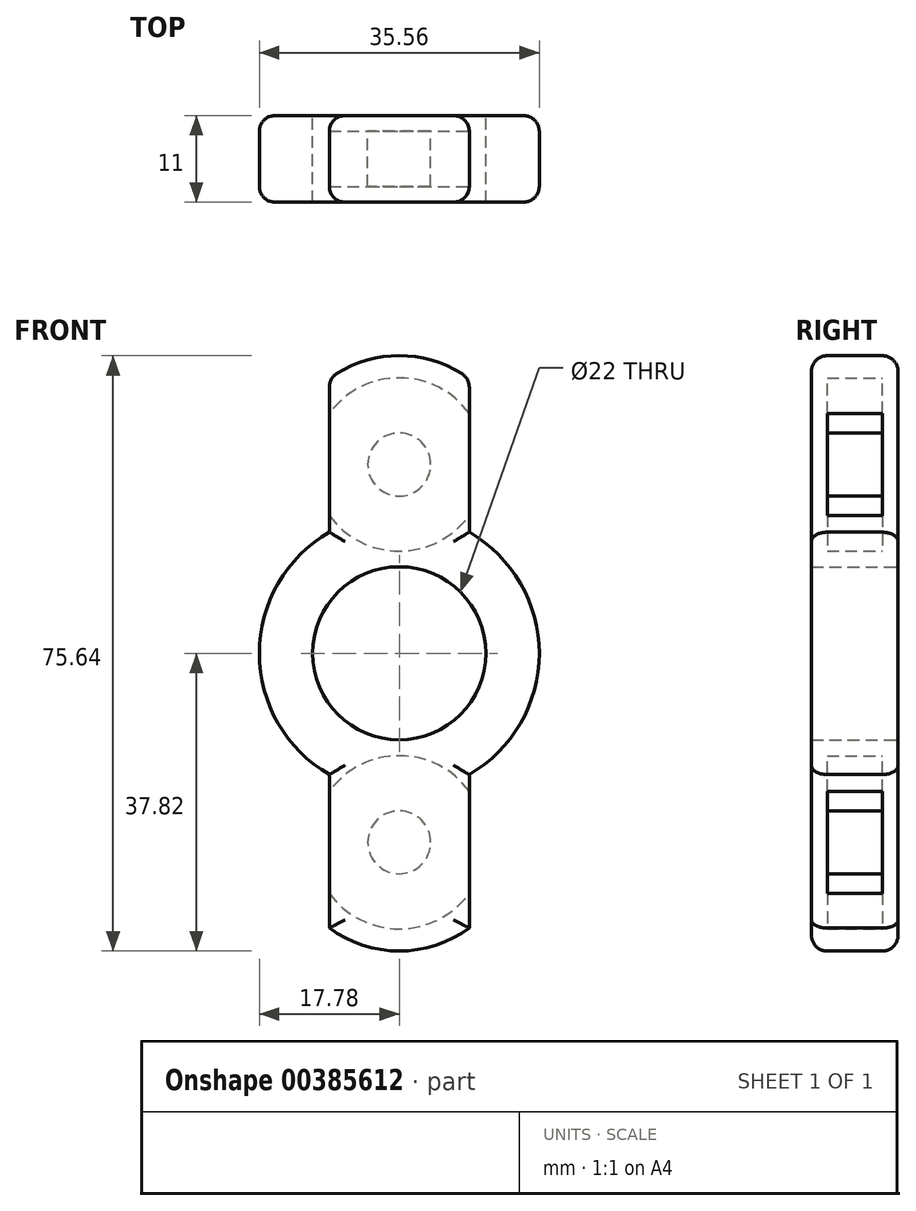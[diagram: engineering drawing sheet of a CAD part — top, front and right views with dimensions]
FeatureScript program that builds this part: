
annotation { "Feature Type Name" : "Feature", "Feature Type Description" : "" }
export const myFeature = defineFeature(function(context is Context, id is Id, definition is map)
    precondition{}
    {
        {
            var Q0;
            Q0=qCreatedBy(makeId("Front.planeOp"),FACE);
            var sketch = newSketch(context, id + "F0", { "sketchPlane" : qUnion([Q0])});
            skArc(sketch, "E0", {"start": v(-8.9, 15.4) * mm, "mid": v(-17.78, 0) * mm, "end": v(-8.9, -15.4) * mm});
            skLineSegment(sketch, "E1", {"start": v(-8.89, 34.9) * mm, "end": v(-8.89, 15.4) * mm});
            skLineSegment(sketch, "E2", {"start": v(8.9, 34.9) * mm, "end": v(8.9, 15.4) * mm});
            skArc(sketch, "E3.trimOffspring", {"start": v(8.9, 34.9) * mm, "mid": v(0, 37.82) * mm, "end": v(-8.89, 34.9) * mm});
            skLineSegment(sketch, "E4.trimOffspring", {"start": v(-8.9, -15.4) * mm, "end": v(-8.9, -34.9) * mm});
            skLineSegment(sketch, "E5.trimOffspring", {"start": v(8.89, -15.4) * mm, "end": v(8.89, -34.9) * mm});
            skArc(sketch, "E6.trimOffspring", {"start": v(8.9, -15.4) * mm, "mid": v(17.78, 0) * mm, "end": v(8.9, 15.4) * mm});
            skArc(sketch, "E7.trimOffspring", {"start": v(-8.9, -34.9) * mm, "mid": v(0, -37.82) * mm, "end": v(8.9, -34.9) * mm});
            skPoint(sketch, "E8.center.orphan", {"position": v(0, -27.75) * mm});
            skLineSegment(sketch, "E9", {"start": v(0, 51.08) * mm, "end": v(0, -57.27) * mm, "construction": true});
            skPoint(sketch, "E10.center.orphan", {"position": v(0, 27.75) * mm});
            skCircle(sketch, "E11", {"center": v(0, 0) * mm, "radius": 11 * mm});
            skSolve(sketch);
        }
        {
            var Q0;
            Q0=qCreatedBy(makeId("Front.planeOp"),FACE);
            var sketch = newSketch(context, id + "F1", { "sketchPlane" : qUnion([Q0])});
            skCircle(sketch, "E12", {"center": v(0, 0) * mm, "radius": 11 * mm});
            skCircle(sketch, "E13", {"center": v(0, 24) * mm, "radius": 11 * mm});
            skLineSegment(sketch, "E14.anchor1", {"start": v(0, -6.37) * mm, "end": v(0, 24) * mm, "construction": true});
            skLineSegment(sketch, "E14.anchor2", {"start": v(0, -9.63) * mm, "end": v(0, -39.63) * mm, "construction": true});
            skCircle(sketch, "E15.1.0", {"center": v(0, -24) * mm, "radius": 11 * mm});
            skCircle(sketch, "E16", {"center": v(0, 24) * mm, "radius": 4 * mm});
            skCircle(sketch, "E17", {"center": v(0, -24) * mm, "radius": 4 * mm});
            skSolve(sketch);
        }
        {
            var Q0;
            Q0=makeQuery(id+"F1.imprint","IMPRINT",FACE,{"disambiguationData":[TD([[makeQuery(id+"F1.imprint","IMPRINT",EDGE,{"derivedFrom":sQuery(id+"F1.wireOp",EDGE,"E13")}),1.0]])]});
            var Q1;
            Q1=makeQuery(id+"F1.imprint","IMPRINT",FACE,{"disambiguationData":[TD([[makeQuery(id+"F1.imprint","IMPRINT",EDGE,{"derivedFrom":sQuery(id+"F1.wireOp",EDGE,"E15.1.0")}),1.0]])]});
            extrude(context, id + "F2", {"entities" : qUnion([Q0, Q1]), "depth" : 7 * mm});
        }
        {
            var Q0;
            Q0 = qSketchRegion(id + "F0", true);
            extrude(context, id + "F3", {"entities" : qUnion([Q0]), "depth" : 9 * mm, "hasSecondDirection" : true, "secondDirectionOppositeDirection" : true, "secondDirectionDepth" : 2 * mm});
        }
        {
            var Q0;
            Q0=makeQuery(id+"F3.opExtrude","CAP_EDGE",EDGE,{"disambiguationData":[OSD([sQuery(id+"F0.wireOp",EDGE,"E1")])],"isStart":false});
            var Q1;
            Q1=makeQuery(id+"F3.opExtrude","CAP_EDGE",EDGE,{"disambiguationData":[OSD([sQuery(id+"F0.wireOp",EDGE,"E0")])],"isStart":false});
            var Q2;
            Q2=makeQuery(id+"F3.opExtrude","CAP_EDGE",EDGE,{"disambiguationData":[OSD([sQuery(id+"F0.wireOp",EDGE,"E2")])],"isStart":false});
            var Q3;
            Q3=makeQuery(id+"F3.opExtrude","CAP_EDGE",EDGE,{"disambiguationData":[OSD([sQuery(id+"F0.wireOp",EDGE,"E6.trimOffspring")])],"isStart":false});
            var Q4;
            Q4=makeQuery(id+"F3.opExtrude","CAP_EDGE",EDGE,{"disambiguationData":[OSD([sQuery(id+"F0.wireOp",EDGE,"E3.trimOffspring")])],"isStart":false});
            var Q5;
            Q5=makeQuery(id+"F3.opExtrude","CAP_EDGE",EDGE,{"disambiguationData":[OSD([sQuery(id+"F0.wireOp",EDGE,"E7.trimOffspring")])],"isStart":false});
            var Q6;
            Q6=makeQuery(id+"F3.opExtrude","CAP_EDGE",EDGE,{"disambiguationData":[OSD([sQuery(id+"F0.wireOp",EDGE,"E5.trimOffspring")])],"isStart":false});
            var Q7;
            Q7=makeQuery(id+"F3.opExtrude","CAP_EDGE",EDGE,{"disambiguationData":[OSD([sQuery(id+"F0.wireOp",EDGE,"E4.trimOffspring")])],"isStart":false});
            var Q8;
            Q8=makeQuery(id+"F3.opExtrude","CAP_EDGE",EDGE,{"disambiguationData":[OSD([sQuery(id+"F0.wireOp",EDGE,"E1")])],"isStart":true});
            var Q9;
            Q9=makeQuery(id+"F3.opExtrude","CAP_EDGE",EDGE,{"disambiguationData":[OSD([sQuery(id+"F0.wireOp",EDGE,"E3.trimOffspring")])],"isStart":true});
            var Q10;
            Q10=makeQuery(id+"F3.opExtrude","CAP_EDGE",EDGE,{"disambiguationData":[OSD([sQuery(id+"F0.wireOp",EDGE,"E0")])],"isStart":true});
            var Q11;
            Q11=makeQuery(id+"F3.opExtrude","CAP_EDGE",EDGE,{"disambiguationData":[OSD([sQuery(id+"F0.wireOp",EDGE,"E4.trimOffspring")])],"isStart":true});
            var Q12;
            Q12=makeQuery(id+"F3.opExtrude","CAP_EDGE",EDGE,{"disambiguationData":[OSD([sQuery(id+"F0.wireOp",EDGE,"E7.trimOffspring")])],"isStart":true});
            var Q13;
            Q13=makeQuery(id+"F3.opExtrude","CAP_EDGE",EDGE,{"disambiguationData":[OSD([sQuery(id+"F0.wireOp",EDGE,"E2")])],"isStart":true});
            var Q14;
            Q14=makeQuery(id+"F3.opExtrude","CAP_EDGE",EDGE,{"disambiguationData":[OSD([sQuery(id+"F0.wireOp",EDGE,"E6.trimOffspring")])],"isStart":true});
            var Q15;
            Q15=makeQuery(id+"F3.opExtrude","CAP_EDGE",EDGE,{"disambiguationData":[OSD([sQuery(id+"F0.wireOp",EDGE,"E5.trimOffspring")])],"isStart":true});
            var Q16;
            Q16=makeQuery(id+"F3.opExtrude","SWEPT_FACE",FACE,{"disambiguationData":[OSD([sQuery(id+"F0.wireOp",EDGE,"E3.trimOffspring")])]});
            fillet(context, id + "F4", {"entities" : qUnion([Q0, Q1, Q2, Q3, Q4, Q5, Q6, Q7, Q8, Q9, Q10, Q11, Q12, Q13, Q14, Q15, Q16]), "radius" : 2 * mm, "tangentPropagation" : true, "allowEdgeOverflow" : false});
        }
        {
            var Q0;
            Q0=makeQuery(id+"F2.opExtrude","SWEPT_BODY",BODY,{"disambiguationData":[OSD([sQuery(id+"F1.wireOp",EDGE,"E13")])]});
            var Q1;
            Q1=makeQuery(id+"F2.opExtrude","SWEPT_BODY",BODY,{"disambiguationData":[OSD([sQuery(id+"F1.wireOp",EDGE,"E15.1.0")])]});
            var Q2;
            Q2=makeQuery(id+"F3.opExtrude","SWEPT_BODY",BODY,{"disambiguationData":[OSD([sQuery(id+"F0.wireOp",EDGE,"E0"),sQuery(id+"F0.wireOp",EDGE,"E1"),sQuery(id+"F0.wireOp",EDGE,"E2"),sQuery(id+"F0.wireOp",EDGE,"E3.trimOffspring"),sQuery(id+"F0.wireOp",EDGE,"E4.trimOffspring"),sQuery(id+"F0.wireOp",EDGE,"E5.trimOffspring"),sQuery(id+"F0.wireOp",EDGE,"E6.trimOffspring"),sQuery(id+"F0.wireOp",EDGE,"E7.trimOffspring"),sQuery(id+"F0.wireOp",EDGE,"E11")])]});
            booleanBodies(context, id + "F5", {"operationType" : BooleanOperationType.SUBTRACTION, "tools" : qUnion([Q0, Q1]), "targets" : qUnion([Q2])});
        }
    });
